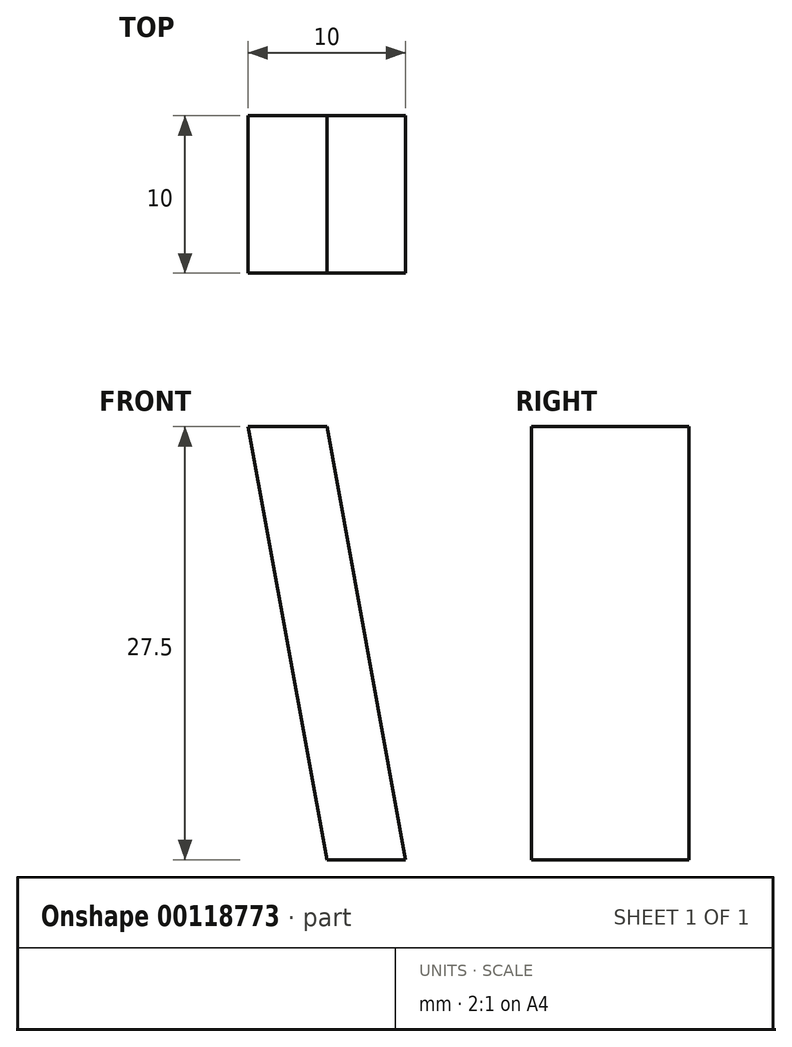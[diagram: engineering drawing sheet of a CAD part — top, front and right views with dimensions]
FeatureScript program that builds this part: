
annotation { "Feature Type Name" : "Feature", "Feature Type Description" : "" }
export const myFeature = defineFeature(function(context is Context, id is Id, definition is map)
    precondition{}
    {
        {
            var Q0;
            Q0=qCreatedBy(makeId("Top.planeOp"),FACE);
            var sketch = newSketch(context, id + "F0", { "sketchPlane" : qUnion([Q0])});
            skLineSegment(sketch, "E0.bottom", {"start": v(2.5, -5) * mm, "end": v(-2.5, -5) * mm});
            skLineSegment(sketch, "E0.top", {"start": v(2.5, 5) * mm, "end": v(-2.5, 5) * mm});
            skLineSegment(sketch, "E0.left", {"start": v(2.5, -5) * mm, "end": v(2.5, 5) * mm});
            skLineSegment(sketch, "E0.right", {"start": v(-2.5, -5) * mm, "end": v(-2.5, 5) * mm});
            skPoint(sketch, "E0.middle", {"position": v(0, 0) * mm});
            skSolve(sketch);
        }
        {
            var Q0;
            Q0=qCreatedBy(makeId("Front.planeOp"),FACE);
            var sketch = newSketch(context, id + "F1", { "sketchPlane" : qUnion([Q0])});
            skLineSegment(sketch, "E1", {"start": v(0, 0) * mm, "end": v(5, -27.5) * mm});
            skSolve(sketch);
        }
        {
            var Q0;
            Q0=makeQuery(id+"F0.imprint","IMPRINT",FACE,{"disambiguationData":[TD([[makeQuery(id+"F0.imprint","IMPRINT",EDGE,{"derivedFrom":sQuery(id+"F0.wireOp",EDGE,"E0.bottom")}),-1.0]])]});
            var Q1;
            Q1=sQuery(id+"F1.wireOp",EDGE,"E1");
            sweep(context, id + "F2", {"profiles" : qUnion([Q0]), "path" : qUnion([Q1])});
        }
    });
